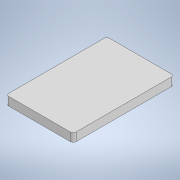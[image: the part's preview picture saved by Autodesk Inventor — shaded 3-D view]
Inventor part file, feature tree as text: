
AUTODESK INVENTOR PART (.ipt)
format: ipt  version: 2022 (Build 260153000, 153)  size: 105,984 bytes
history: native  units: in
note: dims shown in document units (in); Inventor stores cm internally (conversion verified against a paired STEP export)
features: fillet x4, extrude x1, sketch x1
ambient origin geometry x8: Origin, YZ Plane, XZ Plane, XY Plane, X Axis, Y Axis, Z Axis, Center Point
bodies: Solid1 (feature_tree)
feature tree (6):
  extrude  "Extrusion1"  Depth=7.0866in
  fillet  "Face Fillet1"
  fillet  "Face Fillet2"
  fillet  "Face Fillet3"
  fillet  "Face Fillet4"
  sketch  "Sketch1"  dims[d0=4.7244in d1=7.0866in d2=0.5906in d3=0.0in d4=0.1969in d5=0.1969in d6=0.1969in d7=0.1969in]
